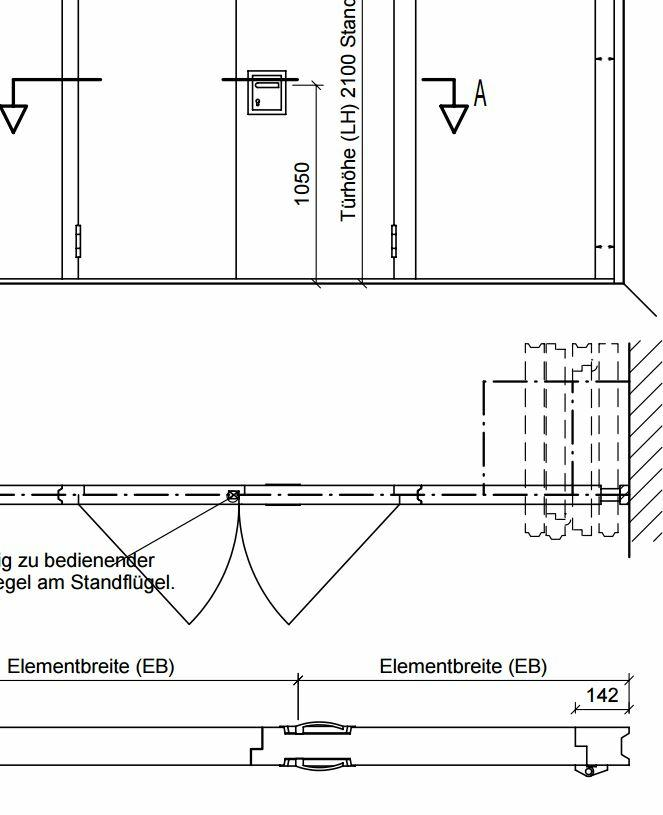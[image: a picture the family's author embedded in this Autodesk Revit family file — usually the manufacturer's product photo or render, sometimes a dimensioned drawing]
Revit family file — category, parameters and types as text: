
# Revit family: Walls_Moving_walls_Komandor_MAW_110_Two_double_door_Z1
name_source: partatom
category: Generic Models
revit_build: Autodesk Revit 2014 (Build: 20130308_1515(x64)
units: mm (PartAtom-declared; Revit-internal decimal feet)

## types (1)
- Walls_Moving_walls_Komandor_MAW_110_Two_double_door_Z1
    1st Bar Distance = 2750 mm  [stored 9.02231 ft]
    2nd Bar Distance = 5500 mm  [stored 18.0446 ft]
    BIMobject category = Folding & Moving Walls
    COBIe Type Category = Wall MOVABLE
    Design country = Poland
    Door Panel Axis = 543 mm
    Edition number = 1
    IFC Classification = Wall
    Installation instructions = http://www.komandorwalls.com
    Manufacturer country = Poland
    Manufacturer name = Komandor
    Masterformat 2014 Code = 07 42 00
    Masterformat 2014 Description = Wall Panels
    Material main = Aluminium
    Material secondary = MDF
    NBS Reference Code = 25-30-20-80
    NBS Reference Description = Sliding Stacking Panel Partition Systems
    Nominal height = 0
    Nominal width = 0
    OmniClass Code = 23-15 13 19
    OmniClass Description = Wall Panels
    Panel Material = Laminate, Pine Avola Brown
    Product Guid = f88639dd-7851-4d73-ba37-f0ca554d38d5
    Product SKU = maw110
    Product data url = https://bimobject.com
    Product family = Walls
    Product group = MAW
    Profile Material = Komandor_Aluminum
    QR code = http://bimobject.com
    UNSPSC Code = 301615
    Uniclass 1.4 Code = L83122
    Uniclass 1.4 Description = Wall units
    Uniclass 2.0 Code = SS-25-30-20-80
    Uniclass 2.0 Description = Sliding Stacking Panel Partition Systems
    Uniclass 2015 Code = EF_25
    Uniclass 2015 Name = Wall and barrier elements
    Uniformat II Code = C3010
    Uniformat II Description = Wall Finishes
    Weight Net (Kg) = 0
    Youtube clip = https://www.youtube.com

note: [stored X ft] marks values corroborated as IEEE doubles in the binary element streams (Revit-internal decimal feet)

## geometry (parser evidence)
native form markers: Sweep x111
no freeform markers — native parametric forms only
